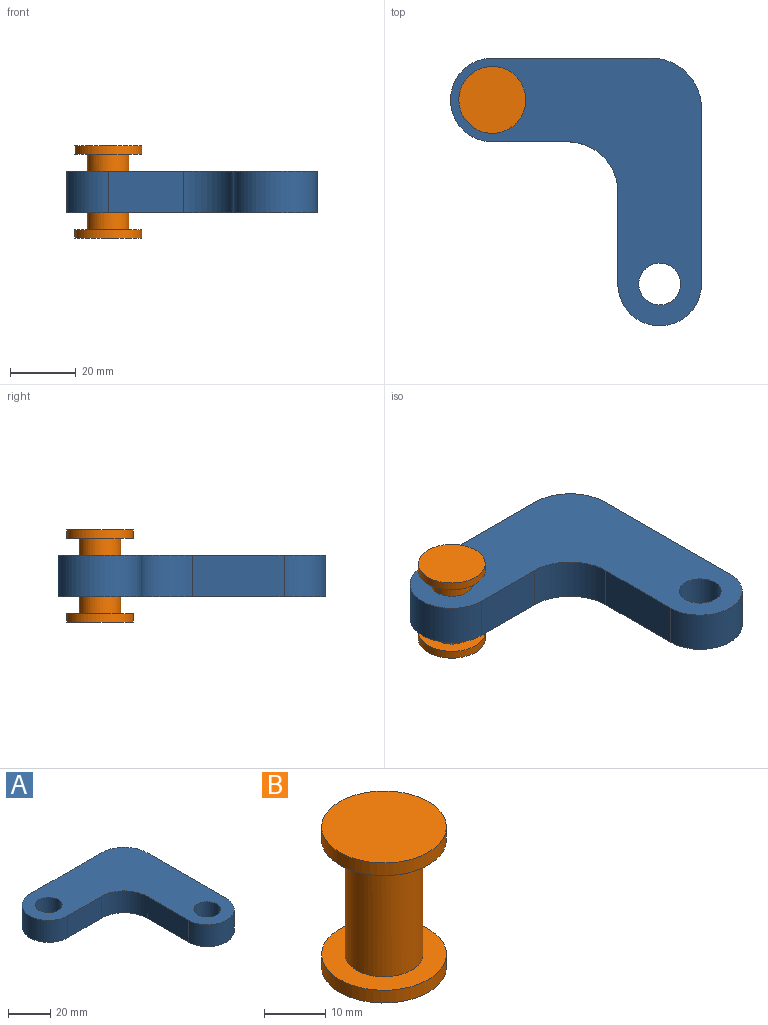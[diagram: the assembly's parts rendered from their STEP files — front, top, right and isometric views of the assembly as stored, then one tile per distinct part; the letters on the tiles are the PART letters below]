
ASSEMBLY  parts=2 mates=1
PART A: 12 faces, bbox 76.2x81.3x12.7 mm
  f0: plane 48.17x12.7mm, normal (0,1,0), area 611.8mm2, adj f1,f8,f9,f11
  f1: cylinder r=12.7mm len=25.4mm, axis (0,0,-1), area 506.7mm2, adj f0,f2,f8,f9
  f2: plane 22.77x12.7mm, normal (0,-1,0), area 289.2mm2, adj f1,f8,f9,f10
  f3: plane 27.85x12.7mm, normal (-1,0,0), area 353.7mm2, adj f4,f8,f9,f10
  f4: cylinder r=12.7mm len=25.4mm, axis (0,0,-1), area 506.7mm2, adj f3,f6,f8,f9
  f5: cylinder r=6.35mm len=12.7mm, axis (0,0,-1), area 506.7mm2, adj f8,f9
  f6: plane 53.25x12.7mm, normal (1,0,0), area 676.3mm2, adj f4,f8,f9,f11
  f7: cylinder r=6.35mm len=12.7mm, axis (0,0,-1), area 506.7mm2, adj f8,f9
  f8: plane 81.28x76.2mm, normal (0,0,1), area 2963mm2, adj f0,f1,f2,f3,f4,f5,f6,f7
  f9: plane 81.28x76.2mm, normal (0,0,-1), area 2963mm2, adj f0,f1,f2,f3,f4,f5,f6,f7
  f10: cylinder r=15.33mm len=15.33mm, axis (0,0,1), area 305.8mm2, adj f2,f3,f8,f9
  f11: cylinder r=15.33mm len=15.33mm, axis (0,0,1), area 305.8mm2, adj f0,f6,f8,f9
PART B: 7 faces, bbox 20.3x20.3x27.9 mm
  f0: cylinder r=6.35mm len=22.86mm, axis (0,0,-1), area 912.1mm2, adj f3,f5
  f1: cylinder r=10.16mm len=20.32mm, axis (0,0,-1), area 162.1mm2, adj f2,f3
  f2: plane 20.32x20.32mm, normal (0,0,1), area 324.3mm2, adj f1
  f3: plane 20.32x20.32mm, normal (0,0,-1), area 197.6mm2, adj f0,f1
  f4: cylinder r=10.16mm len=20.32mm, axis (0,0,-1), area 162.1mm2, adj f5,f6
  f5: plane 20.32x20.32mm, normal (0,0,1), area 197.6mm2, adj f0,f4
  f6: plane 20.32x20.32mm, normal (0,0,-1), area 324.3mm2, adj f4
PLACE A t=(-29.93,-11.09,23.26)mm
PLACE B t=(-29.93,1.61,15.64)mm
MATE revolute A.f7 <-> B.f0  axis (0,0,-1) through (-29.93,1.61,29.61)mm
